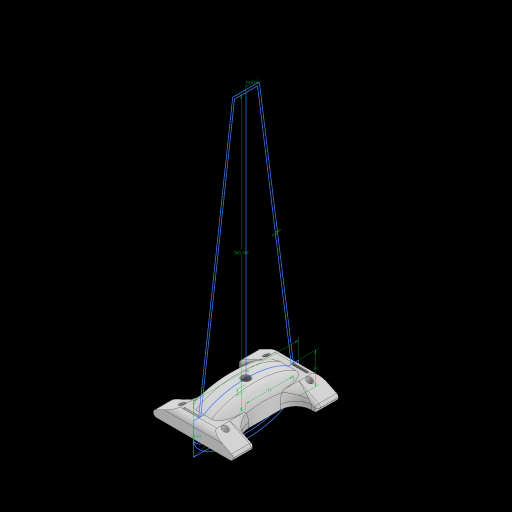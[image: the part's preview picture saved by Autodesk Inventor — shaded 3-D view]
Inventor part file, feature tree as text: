
AUTODESK INVENTOR PART (.ipt)
format: ipt  version: 2023 (Build 270158000, 158)  size: 613,888 bytes
history: native  units: mm
features: extrude x6, fillet x6, chamfer x4, sketch x2, hole x1
ambient origin geometry x8: Origin, YZ Plane, XZ Plane, XY Plane, X Axis, Y Axis, Z Axis, Center Point
bodies: Solid1 (feature_tree)
feature tree (19):
  sketch  "Sketch2"  dims[d2=260.34779mm d3=45.0mm d4=10.93871mm d5=2.0mm d7=30.0mm]
  sketch  "Sketch3"  dims[d8=100.0mm d9=5.0mm d10=5.5mm d11=15.0mm d12=20.0mm d13=35.0mm d14=7.5mm d15=244.423mm d16=41.005864mm d17=18.0mm d18=264.926mm d19=0.0mm d20=15.0mm d21=35.0mm d22=0.0mm d27=15.0mm d28=0.0mm d29=20.5mm d30=10.0mm d31=45.0deg d32=20.5mm d33=10.0mm d34=45.0deg d35=20.5mm d36=10.0mm d37=45.0deg d38=20.5mm d39=10.0mm d40=45.0deg d43=90.0deg d44=5.0mm d45=3.0mm d46=3.0mm d47=3.0mm d48=2.0mm d49=0.0mm d52=15.0mm d53=0.0mm d54=8.0mm d55=6.0mm d56=17.3mm d57=2.0mm d58=90.0deg d59=30.0mm d60=0.0mm d68=10.0mm d69=15.0mm d70=0.0mm d71=15.0mm d72=0.0mm d73=15.0mm]
  extrude  "Extrusion1"  Depth=30.0mm
  extrude  "Extrusion4"  Depth=15.0mm
  chamfer  "Chamfer1"  Distance=35.0mm
  chamfer  "Chamfer2"  Distance=15.0mm
  chamfer  "Chamfer3"  Distance=10.0mm Angle=45.0deg
  chamfer  "Chamfer4"  Distance=10.0mm Angle=45.0deg
  fillet  "Fillet3"  Radius=10.0mm
  fillet  "Fillet4"  Radius=10.0mm
  fillet  "Fillet5"  [1 undecoded]
  fillet  "Fillet6"  Radius=5.0mm
  extrude  "Extrusion5"  Depth=15.0mm
  extrude  "Extrusion7"  Depth=15.0mm
  hole  "Hole1"  [1 undecoded]
  fillet  "Fillet7"  Radius=2.0mm
  extrude  "Extrusion8"  Depth=15.0mm TaperAngle=0.0deg
  extrude  "Extrusion9"  Depth=10.0mm
  fillet  "Fillet8"  Radius=15.0mm
note: 2 required parameter values undecoded (feature->parameter linkage not recoverable at this tier; creation-order binding heuristic only, values carry confidence <= 0.55)
